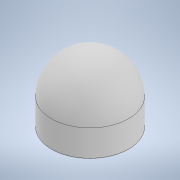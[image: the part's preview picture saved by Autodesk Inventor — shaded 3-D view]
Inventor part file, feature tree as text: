
AUTODESK INVENTOR PART (.ipt)
format: ipt  version: 2020 (Build 240168000, 168)  size: 155,136 bytes
history: native  units: in
note: dims shown in document units (in); Inventor stores cm internally (conversion verified against a paired STEP export)
features: fillet x2, revolve x1, sketch x1
ambient origin geometry x8: Origin, YZ Plane, XZ Plane, XY Plane, X Axis, Y Axis, Z Axis, Center Point
bodies: Solid1 (feature_tree)
feature tree (4):
  revolve  "Revolution1"  [1 undecoded]
  fillet  "Fillet1"  Radius=1.2795in
  fillet  "Fillet2"  Radius=0.0787in
  sketch  "Sketch1"  dims[d0=2.2441in d1=0.0787in d2=1.2795in d3=0.0787in d4=1.2795in d5=90.0deg d6=0.0394in d7=0.0394in]
note: 1 required parameter value undecoded (feature->parameter linkage not recoverable at this tier; creation-order binding heuristic only, values carry confidence <= 0.55)
